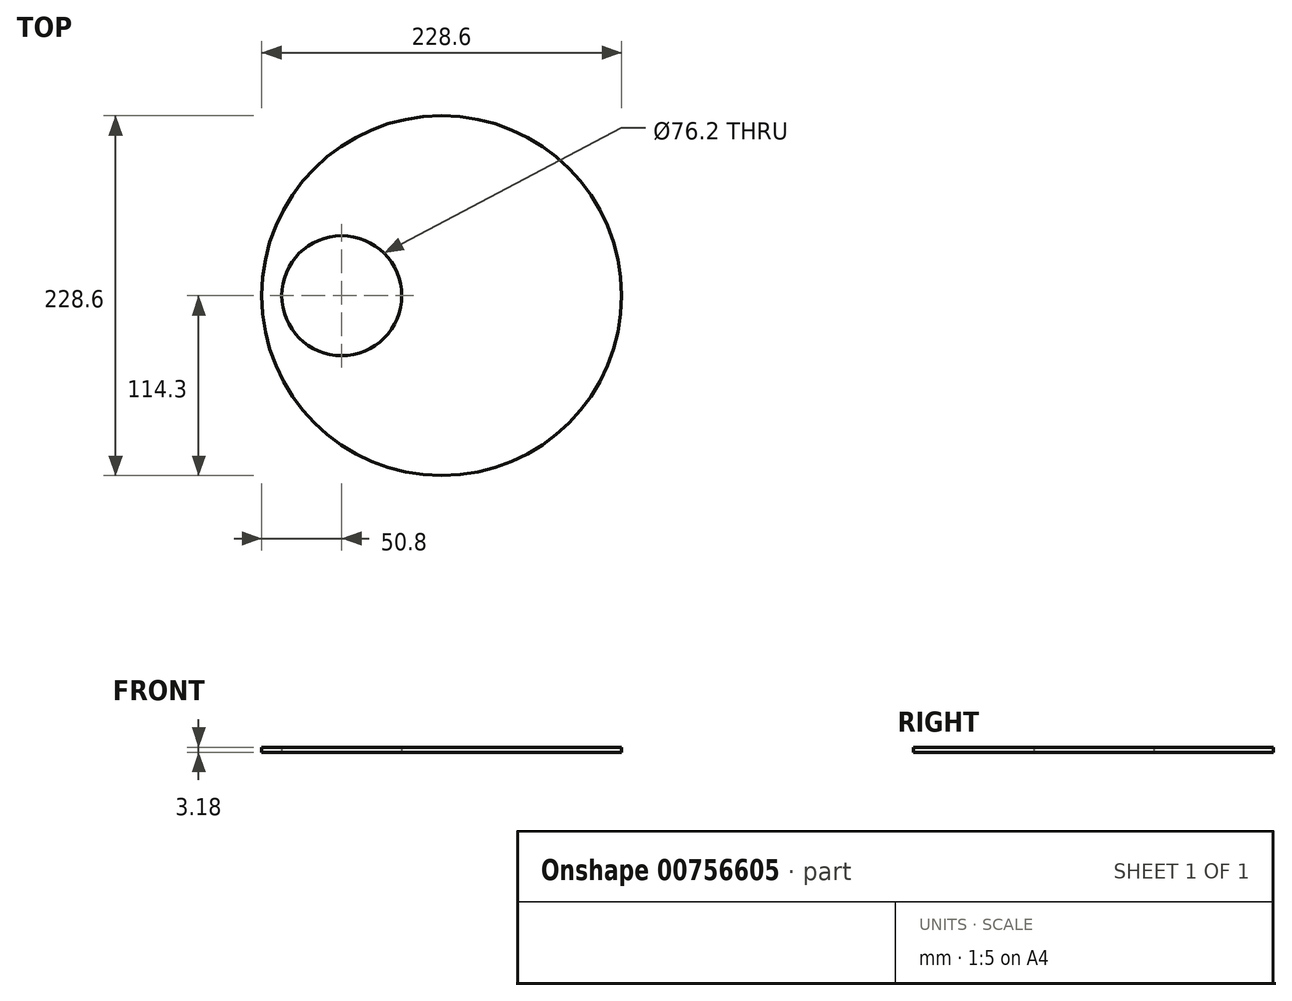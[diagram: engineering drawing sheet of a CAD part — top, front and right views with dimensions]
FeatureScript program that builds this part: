
annotation { "Feature Type Name" : "Feature", "Feature Type Description" : "" }
export const myFeature = defineFeature(function(context is Context, id is Id, definition is map)
    precondition{}
    {
        {
            var Q0;
            Q0=qCreatedBy(makeId("Top.planeOp"),FACE);
            var sketch = newSketch(context, id + "F0", { "sketchPlane" : qUnion([Q0])});
            skCircle(sketch, "E0", {"center": v(0, 0) * mm, "radius": 114.3 * mm});
            skCircle(sketch, "E1", {"center": v(-63.5, 0) * mm, "radius": 38.1 * mm});
            skLineSegment(sketch, "E2", {"start": v(-63.5, 0) * mm, "end": v(63.5, 0) * mm});
            skSolve(sketch);
        }
        {
            var Q0;
            Q0=makeQuery(id+"F0.imprint","IMPRINT",FACE,{"disambiguationData":[TD([[makeQuery(id+"F0.imprint","IMPRINT",EDGE,{"derivedFrom":sQuery(id+"F0.wireOp",EDGE,"E0")}),1.0]])]});
            extrude(context, id + "F1", {"entities" : qUnion([Q0]), "depth" : 3.17 * mm});
        }
    });
